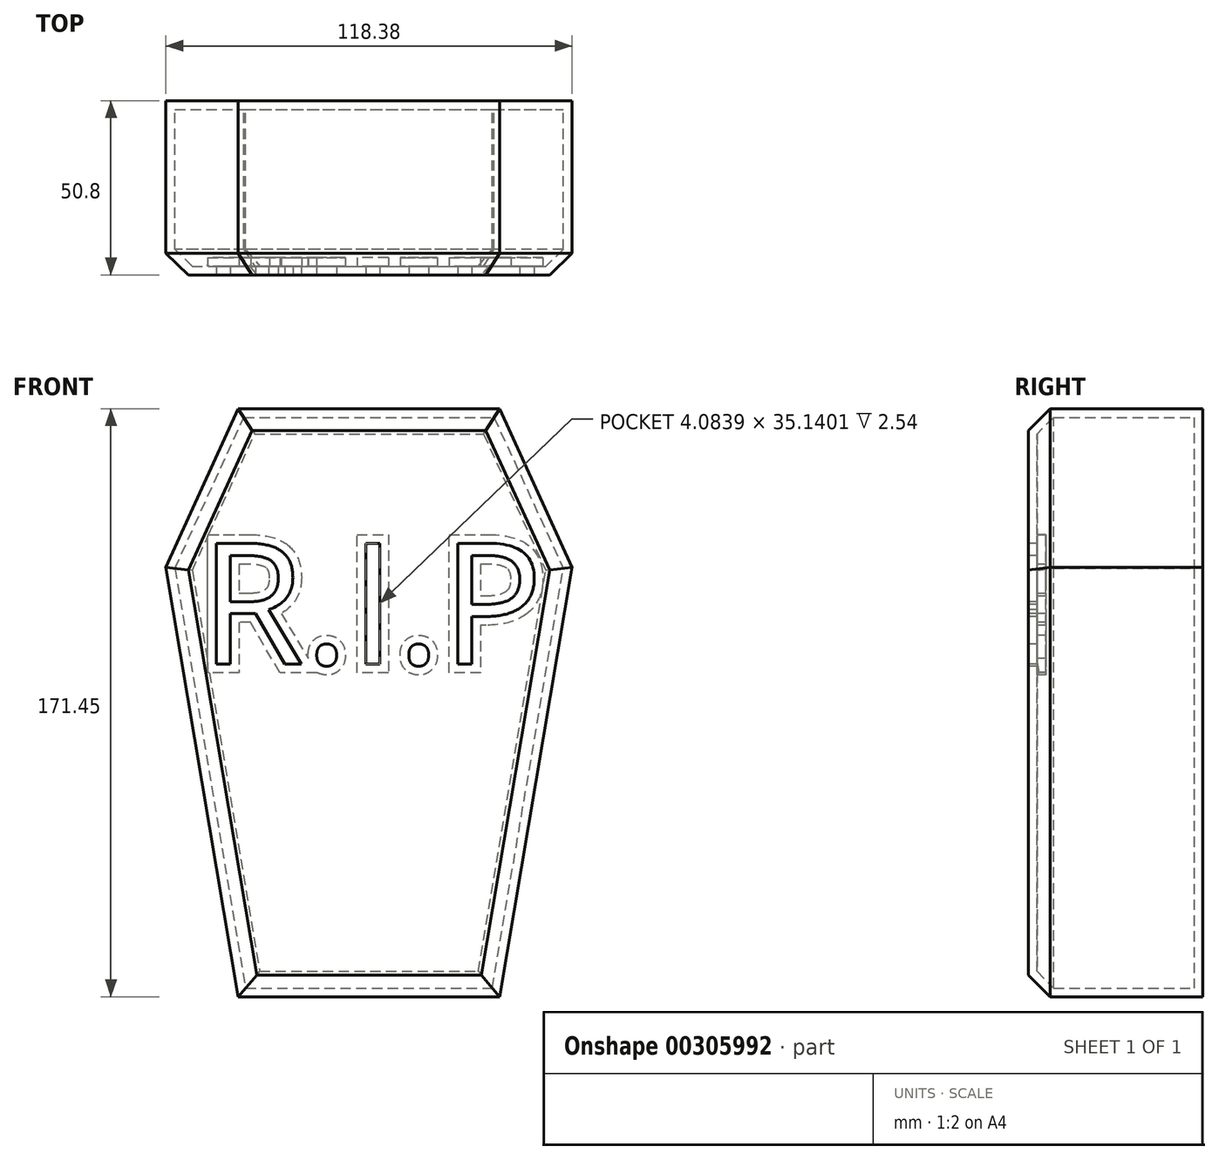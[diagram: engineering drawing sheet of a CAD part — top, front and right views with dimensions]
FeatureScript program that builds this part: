
annotation { "Feature Type Name" : "Feature", "Feature Type Description" : "" }
export const myFeature = defineFeature(function(context is Context, id is Id, definition is map)
    precondition{}
    {
        {
            var Q0;
            Q0=qCreatedBy(makeId("Front.planeOp"),FACE);
            var sketch = newSketch(context, id + "F0", { "sketchPlane" : qUnion([Q0])});
            skLineSegment(sketch, "E0", {"start": v(-35.6, -61.9) * mm, "end": v(40.6, -61.9) * mm});
            skLineSegment(sketch, "E1", {"start": v(40.6, -61.9) * mm, "end": v(61.69, 63.34) * mm});
            skLineSegment(sketch, "E2", {"start": v(-56.7, 63.34) * mm, "end": v(-35.6, -61.9) * mm});
            skLineSegment(sketch, "E3", {"start": v(-56.7, 63.34) * mm, "end": v(-35.6, 109.56) * mm});
            skLineSegment(sketch, "E4", {"start": v(-35.6, 109.56) * mm, "end": v(40.6, 109.56) * mm});
            skLineSegment(sketch, "E5", {"start": v(40.6, 109.56) * mm, "end": v(61.69, 63.34) * mm});
            skSolve(sketch);
        }
        {
            var Q0;
            Q0=makeQuery(id+"F0.imprint","IMPRINT",FACE,{"disambiguationData":[TD([[makeQuery(id+"F0.imprint","IMPRINT",EDGE,{"derivedFrom":sQuery(id+"F0.wireOp",EDGE,"E0")}),1.0]])]});
            extrude(context, id + "F1", {"entities" : qUnion([Q0]), "depth" : 50.8 * mm});
        }
        {
            var Q0;
            Q0=makeQuery(id+"F1.opExtrude","CAP_FACE",FACE,{"disambiguationData":[OSD([sQuery(id+"F0.wireOp",EDGE,"E0"),sQuery(id+"F0.wireOp",EDGE,"E1"),sQuery(id+"F0.wireOp",EDGE,"E2"),sQuery(id+"F0.wireOp",EDGE,"E3"),sQuery(id+"F0.wireOp",EDGE,"E4"),sQuery(id+"F0.wireOp",EDGE,"E5")])],"isStart":false});
            chamfer(context, id + "F2", {"entities" : qUnion([Q0]), "width" : 6.35 * mm, "tangentPropagation" : true});
        }
        {
            var Q0;
            Q0=makeQuery(id+"F1.opExtrude","CAP_FACE",FACE,{"disambiguationData":[OSD([sQuery(id+"F0.wireOp",EDGE,"E0"),sQuery(id+"F0.wireOp",EDGE,"E1"),sQuery(id+"F0.wireOp",EDGE,"E2"),sQuery(id+"F0.wireOp",EDGE,"E3"),sQuery(id+"F0.wireOp",EDGE,"E4"),sQuery(id+"F0.wireOp",EDGE,"E5")])],"isStart":false});
            var sketch = newSketch(context, id + "F3", { "sketchPlane" : qUnion([Q0])});
            skText(sketch, "E6", { "text": "R.I.P", "fontName": "OpenSans-Regular.ttf"});
            const initialGuessF3  = {"E6": [-0.04681, 0.03515, 1, 0, 0.03544]};
            skSetInitialGuess(sketch, initialGuessF3);
            skSolve(sketch);
        }
        {
            var Q0;
            Q0 = qSketchRegion(id + "F3", true);
            extrude(context, id + "F4", {"entities" : qUnion([Q0]), "operationType" : NewBodyOperationType.REMOVE, "oppositeDirection" : true, "depth" : 2.54 * mm});
        }
        {
            var Q0;
            {var subQ0=sQuery(id+"F0.wireOp",EDGE,"E3");var subQ1=sQuery(id+"F0.wireOp",EDGE,"E2");var subQ2=sQuery(id+"F0.wireOp",EDGE,"E1");var subQ3=sQuery(id+"F0.wireOp",EDGE,"E0");var subQ4=sQuery(id+"F0.wireOp",EDGE,"E4");var subQ5=sQuery(id+"F0.wireOp",EDGE,"E5");Q0=makeQuery(id+"F4.boolean.opBoolean","SPLIT",FACE,{"disambiguationData":[TD([makeQuery(id+"F2.opChamfer","BLEND_FACE",FACE,{"disambiguationData":[OSD([subQ3])]})])],"derivedFrom":makeQuery(id+"F1.opExtrude","CAP_FACE",FACE,{"disambiguationData":[OSD([subQ3,subQ2,subQ1,subQ0,subQ4,subQ5])],"isStart":false})});}
            var Q1;
            Q1=makeQuery(id+"F1.opExtrude","SWEPT_BODY",BODY,{"disambiguationData":[OSD([sQuery(id+"F0.wireOp",EDGE,"E0"),sQuery(id+"F0.wireOp",EDGE,"E1"),sQuery(id+"F0.wireOp",EDGE,"E2"),sQuery(id+"F0.wireOp",EDGE,"E3"),sQuery(id+"F0.wireOp",EDGE,"E4"),sQuery(id+"F0.wireOp",EDGE,"E5")])]});
            shell(context, id + "F5", {"isHollow" : true, "entities" : qUnion([Q0]), "parts" : qUnion([Q1]), "thickness" : 2.54 * mm});
        }
    });
